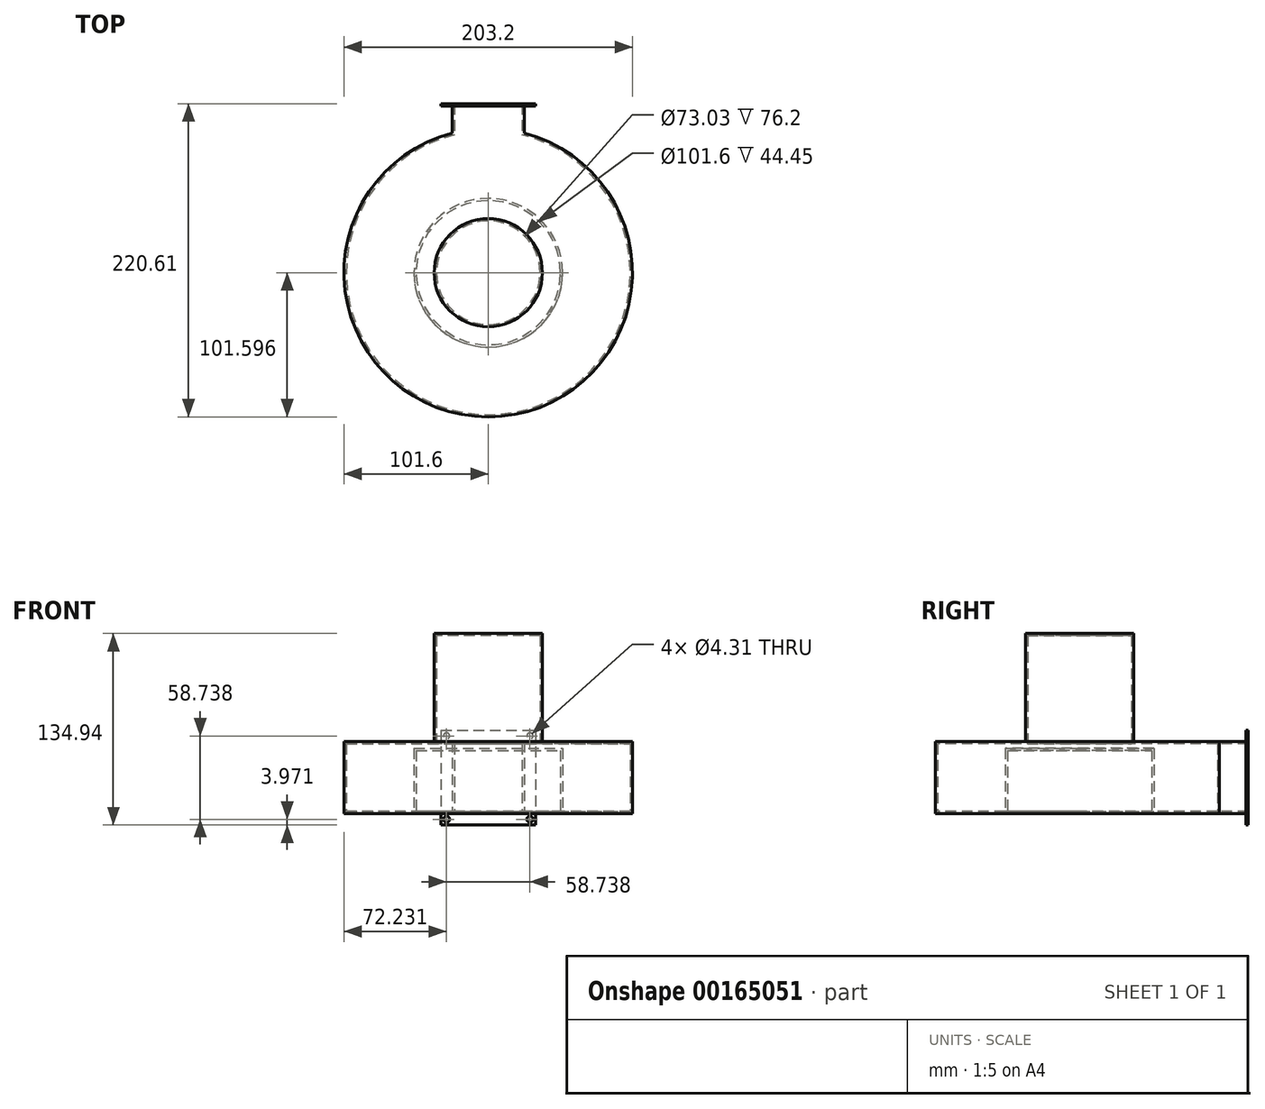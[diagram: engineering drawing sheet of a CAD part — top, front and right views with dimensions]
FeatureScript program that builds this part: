
annotation { "Feature Type Name" : "Feature", "Feature Type Description" : "" }
export const myFeature = defineFeature(function(context is Context, id is Id, definition is map)
    precondition{}
    {
        {
            var Q0;
            Q0=qCreatedBy(makeId("Top.planeOp"),FACE);
            var sketch = newSketch(context, id + "F0", { "sketchPlane" : qUnion([Q0])});
            skLineSegment(sketch, "E0.bottom", {"start": v(0, 0) * mm, "end": v(50.8, 0) * mm});
            skLineSegment(sketch, "E0.top", {"start": v(0, -19.05) * mm, "end": v(50.8, -19.05) * mm, "construction": true});
            skLineSegment(sketch, "E0.left", {"start": v(0, 0) * mm, "end": v(0, -19.05) * mm});
            skLineSegment(sketch, "E0.right", {"start": v(50.8, 0) * mm, "end": v(50.8, -19.05) * mm});
            skLineSegment(sketch, "E1", {"start": v(25.4, -19.05) * mm, "end": v(25.4, -117.42) * mm, "construction": true});
            skArc(sketch, "E2", {"start": v(0, -19.05) * mm, "mid": v(25.4, -219.02) * mm, "end": v(50.8, -19.05) * mm});
            skSolve(sketch);
        }
        {
            var Q0;
            Q0 = qSketchRegion(id + "F0", true);
            extrude(context, id + "F1", {"entities" : qUnion([Q0]), "depth" : 50.8 * mm});
        }
        {
            var Q0;
            Q0=makeQuery(id+"F1.opExtrude","CAP_FACE",FACE,{"disambiguationData":[OSD([sQuery(id+"F0.wireOp",EDGE,"E0.bottom"),sQuery(id+"F0.wireOp",EDGE,"E0.left"),sQuery(id+"F0.wireOp",EDGE,"E0.right"),sQuery(id+"F0.wireOp",EDGE,"E2")])],"isStart":false});
            var sketch = newSketch(context, id + "F2", { "sketchPlane" : qUnion([Q0])});
            skCircle(sketch, "E3", {"center": v(25.4, -117.42) * mm, "radius": 38.1 * mm});
            skSolve(sketch);
        }
        {
            var Q0;
            Q0 = qSketchRegion(id + "F2", true);
            extrude(context, id + "F3", {"entities" : qUnion([Q0]), "operationType" : NewBodyOperationType.ADD, "depth" : 76.2 * mm});
        }
        {
            var Q0;
            Q0=makeQuery(id+"F1.opExtrude","CAP_FACE",FACE,{"disambiguationData":[OSD([sQuery(id+"F0.wireOp",EDGE,"E0.bottom"),sQuery(id+"F0.wireOp",EDGE,"E0.left"),sQuery(id+"F0.wireOp",EDGE,"E0.right"),sQuery(id+"F0.wireOp",EDGE,"E2")])],"isStart":true});
            var sketch = newSketch(context, id + "F4", { "sketchPlane" : qUnion([Q0])});
            skCircle(sketch, "E4", {"center": v(25.4, 117.42) * mm, "radius": 50.8 * mm});
            skSolve(sketch);
        }
        {
            var Q0;
            Q0 = qSketchRegion(id + "F4", true);
            extrude(context, id + "F5", {"entities" : qUnion([Q0]), "operationType" : NewBodyOperationType.REMOVE, "oppositeDirection" : true, "depth" : 44.45 * mm});
        }
        {
            var Q0;
            Q0=makeQuery(id+"F1.opExtrude","SWEPT_FACE",FACE,{"disambiguationData":[OSD([sQuery(id+"F0.wireOp",EDGE,"E0.bottom")])]});
            shell(context, id + "F6", {"entities" : qUnion([Q0]), "thickness" : 1.59 * mm});
        }
        {
            var Q0;
            Q0=makeQuery(id+"F1.opExtrude","SWEPT_FACE",FACE,{"disambiguationData":[OSD([sQuery(id+"F0.wireOp",EDGE,"E0.bottom")])]});
            var sketch = newSketch(context, id + "F7", { "sketchPlane" : qUnion([Q0])});
            skLineSegment(sketch, "E5", {"start": v(-25.4, 49.21) * mm, "end": v(-25.4, 1.59) * mm, "construction": true});
            skLineSegment(sketch, "E6.bottom", {"start": v(3.97, 54.77) * mm, "end": v(-54.77, 54.77) * mm, "construction": true});
            skLineSegment(sketch, "E6.top", {"start": v(3.97, -3.97) * mm, "end": v(-54.77, -3.97) * mm, "construction": true});
            skLineSegment(sketch, "E6.left", {"start": v(3.97, 54.77) * mm, "end": v(3.97, -3.97) * mm, "construction": true});
            skLineSegment(sketch, "E6.right", {"start": v(-54.77, 54.77) * mm, "end": v(-54.77, -3.97) * mm, "construction": true});
            skPoint(sketch, "E6.middle", {"position": v(-25.4, 25.4) * mm});
            skLineSegment(sketch, "E7", {"start": v(-25.4, 50.8) * mm, "end": v(-25.4, 54.77) * mm, "construction": true});
            skLineSegment(sketch, "E8", {"start": v(-25.4, 54.77) * mm, "end": v(-25.4, 58.74) * mm, "construction": true});
            skLineSegment(sketch, "E9.bottom", {"start": v(7.94, 58.74) * mm, "end": v(-58.74, 58.74) * mm});
            skLineSegment(sketch, "E9.top", {"start": v(7.94, -7.94) * mm, "end": v(-58.74, -7.94) * mm});
            skLineSegment(sketch, "E9.left", {"start": v(7.94, 58.74) * mm, "end": v(7.94, -7.94) * mm});
            skLineSegment(sketch, "E9.right", {"start": v(-58.74, 58.74) * mm, "end": v(-58.74, -7.94) * mm});
            skCircle(sketch, "E10", {"center": v(-54.77, 54.77) * mm, "radius": 2.15 * mm});
            skCircle(sketch, "E11", {"center": v(3.97, 54.77) * mm, "radius": 2.15 * mm});
            skCircle(sketch, "E12", {"center": v(3.97, -3.97) * mm, "radius": 2.15 * mm});
            skCircle(sketch, "E13", {"center": v(-54.77, -3.97) * mm, "radius": 2.15 * mm});
            skLineSegment(sketch, "E14.bottom", {"start": v(-1.59, 49.21) * mm, "end": v(-49.21, 49.21) * mm});
            skLineSegment(sketch, "E14.top", {"start": v(-1.59, 1.59) * mm, "end": v(-49.21, 1.59) * mm});
            skLineSegment(sketch, "E14.left", {"start": v(-1.59, 49.21) * mm, "end": v(-1.59, 1.59) * mm});
            skLineSegment(sketch, "E14.right", {"start": v(-49.21, 49.21) * mm, "end": v(-49.21, 1.59) * mm});
            skSolve(sketch);
        }
        {
            var Q0;
            Q0 = qSketchRegion(id + "F7", true);
            extrude(context, id + "F8", {"entities" : qUnion([Q0]), "operationType" : NewBodyOperationType.ADD, "depth" : 1.59 * mm});
        }
    });
